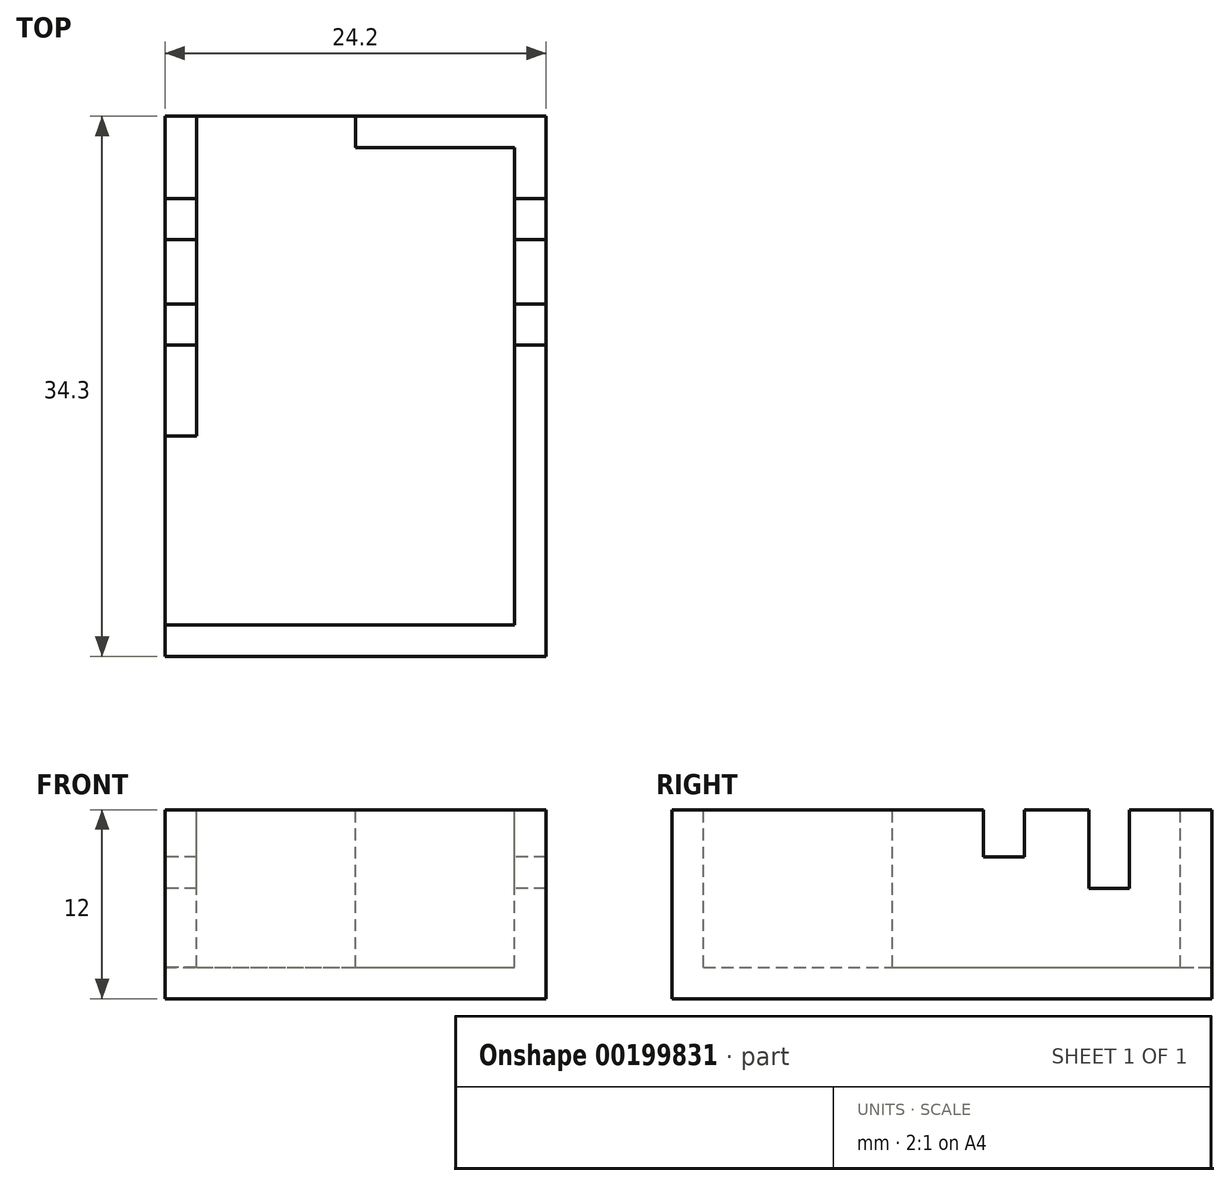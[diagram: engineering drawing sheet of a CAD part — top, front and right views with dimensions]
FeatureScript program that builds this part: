
annotation { "Feature Type Name" : "Feature", "Feature Type Description" : "" }
export const myFeature = defineFeature(function(context is Context, id is Id, definition is map)
    precondition{}
    {
        {
            var Q0;
            Q0=qCreatedBy(makeId("Top.planeOp"),FACE);
            var sketch = newSketch(context, id + "F0", { "sketchPlane" : qUnion([Q0])});
            skLineSegment(sketch, "E0.bottom", {"start": v(0, 0) * mm, "end": v(24.2, 0) * mm});
            skLineSegment(sketch, "E0.top", {"start": v(0, 34.3) * mm, "end": v(24.2, 34.3) * mm});
            skLineSegment(sketch, "E0.left", {"start": v(0, 0) * mm, "end": v(0, 34.3) * mm});
            skLineSegment(sketch, "E0.right", {"start": v(24.2, 0) * mm, "end": v(24.2, 34.3) * mm});
            skSolve(sketch);
        }
        {
            var Q0;
            Q0=makeQuery(id+"F0.imprint","IMPRINT",FACE,{"disambiguationData":[TD([[makeQuery(id+"F0.imprint","IMPRINT",EDGE,{"derivedFrom":sQuery(id+"F0.wireOp",EDGE,"E0.bottom")}),1.0]])]});
            extrude(context, id + "F1", {"entities" : qUnion([Q0]), "depth" : 12 * mm});
        }
        {
            var Q0;
            Q0=makeQuery(id+"F1.opExtrude","CAP_FACE",FACE,{"disambiguationData":[OSD([sQuery(id+"F0.wireOp",EDGE,"E0.bottom"),sQuery(id+"F0.wireOp",EDGE,"E0.top"),sQuery(id+"F0.wireOp",EDGE,"E0.left"),sQuery(id+"F0.wireOp",EDGE,"E0.right")])],"isStart":false});
            var sketch = newSketch(context, id + "F2", { "sketchPlane" : qUnion([Q0])});
            skLineSegment(sketch, "E1.0", {"start": v(2, 32.3) * mm, "end": v(22.2, 32.3) * mm});
            skLineSegment(sketch, "E1.1", {"start": v(2, 2) * mm, "end": v(2, 32.3) * mm});
            skLineSegment(sketch, "E1.2", {"start": v(2, 2) * mm, "end": v(22.2, 2) * mm});
            skLineSegment(sketch, "E1.3", {"start": v(22.2, 2) * mm, "end": v(22.2, 32.3) * mm});
            skSolve(sketch);
        }
        {
            var Q0;
            Q0 = qSketchRegion(id + "F2", true);
            extrude(context, id + "F3", {"entities" : qUnion([Q0]), "operationType" : NewBodyOperationType.REMOVE, "oppositeDirection" : true, "depth" : 10 * mm});
        }
        {
            var Q0;
            Q0=makeQuery(id+"F1.opExtrude","CAP_FACE",FACE,{"disambiguationData":[OSD([sQuery(id+"F0.wireOp",EDGE,"E0.bottom"),sQuery(id+"F0.wireOp",EDGE,"E0.top"),sQuery(id+"F0.wireOp",EDGE,"E0.left"),sQuery(id+"F0.wireOp",EDGE,"E0.right")])],"isStart":false});
            var sketch = newSketch(context, id + "F4", { "sketchPlane" : qUnion([Q0])});
            skLineSegment(sketch, "E2.bottom", {"start": v(2, 2) * mm, "end": v(0, 2) * mm});
            skLineSegment(sketch, "E2.top", {"start": v(2, 14) * mm, "end": v(0, 14) * mm});
            skLineSegment(sketch, "E2.left", {"start": v(2, 2) * mm, "end": v(2, 14) * mm});
            skLineSegment(sketch, "E2.right", {"start": v(0, 2) * mm, "end": v(0, 14) * mm});
            skSolve(sketch);
        }
        {
            var Q0;
            Q0 = qSketchRegion(id + "F4", true);
            extrude(context, id + "F5", {"entities" : qUnion([Q0]), "operationType" : NewBodyOperationType.REMOVE, "oppositeDirection" : true, "depth" : 10 * mm});
        }
        {
            var Q0;
            Q0=makeQuery(id+"F1.opExtrude","CAP_FACE",FACE,{"disambiguationData":[OSD([sQuery(id+"F0.wireOp",EDGE,"E0.bottom"),sQuery(id+"F0.wireOp",EDGE,"E0.top"),sQuery(id+"F0.wireOp",EDGE,"E0.left"),sQuery(id+"F0.wireOp",EDGE,"E0.right")])],"isStart":false});
            var sketch = newSketch(context, id + "F6", { "sketchPlane" : qUnion([Q0])});
            skLineSegment(sketch, "E3.bottom", {"start": v(2, 32.3) * mm, "end": v(12.1, 32.3) * mm});
            skLineSegment(sketch, "E3.top", {"start": v(2, 34.3) * mm, "end": v(12.1, 34.3) * mm});
            skLineSegment(sketch, "E3.left", {"start": v(2, 32.3) * mm, "end": v(2, 34.3) * mm});
            skLineSegment(sketch, "E3.right", {"start": v(12.1, 32.3) * mm, "end": v(12.1, 34.3) * mm});
            skSolve(sketch);
        }
        {
            var Q0;
            Q0 = qSketchRegion(id + "F6", true);
            extrude(context, id + "F7", {"entities" : qUnion([Q0]), "operationType" : NewBodyOperationType.REMOVE, "oppositeDirection" : true, "depth" : 10 * mm});
        }
        {
            var Q0;
            {var subQ0=sQuery(id+"F0.wireOp",EDGE,"E0.right");var subQ1=sQuery(id+"F0.wireOp",EDGE,"E0.left");var subQ2=sQuery(id+"F0.wireOp",EDGE,"E0.top");var subQ3=sQuery(id+"F0.wireOp",EDGE,"E0.bottom");Q0=makeQuery(id+"F7.boolean.opBoolean","SPLIT",FACE,{"disambiguationData":[TD([makeQuery(id+"F1.opExtrude","SWEPT_FACE",FACE,{"disambiguationData":[OSD([subQ3])]})])],"derivedFrom":makeQuery(id+"F1.opExtrude","CAP_FACE",FACE,{"disambiguationData":[OSD([subQ3,subQ2,subQ1,subQ0])],"isStart":false})});}
            var sketch = newSketch(context, id + "F8", { "sketchPlane" : qUnion([Q0])});
            skLineSegment(sketch, "E4.bottom", {"start": v(24.2, 29.07) * mm, "end": v(0, 29.07) * mm});
            skLineSegment(sketch, "E4.top", {"start": v(24.2, 26.47) * mm, "end": v(0, 26.47) * mm});
            skLineSegment(sketch, "E4.left", {"start": v(24.2, 29.07) * mm, "end": v(24.2, 26.47) * mm});
            skLineSegment(sketch, "E4.right", {"start": v(0, 29.07) * mm, "end": v(0, 26.47) * mm});
            skSolve(sketch);
        }
        {
            var Q0;
            Q0 = qSketchRegion(id + "F8", true);
            extrude(context, id + "F9", {"entities" : qUnion([Q0]), "operationType" : NewBodyOperationType.REMOVE, "oppositeDirection" : true, "depth" : 5 * mm});
        }
        {
            var Q0;
            {var subQ1=sQuery(id+"F0.wireOp",EDGE,"E0.right");var subQ3=sQuery(id+"F0.wireOp",EDGE,"E0.left");var subQ5=sQuery(id+"F0.wireOp",EDGE,"E0.bottom");var subQ6=makeQuery(id+"F1.opExtrude","SWEPT_FACE",FACE,{"disambiguationData":[OSD([subQ5])]});var subQ9=sQuery(id+"F0.wireOp",EDGE,"E0.top");Q0=makeQuery(id+"F9.boolean.opBoolean","SPLIT",FACE,{"disambiguationData":[TD([subQ6])],"derivedFrom":makeQuery(id+"F7.boolean.opBoolean","SPLIT",FACE,{"disambiguationData":[TD([subQ6])],"derivedFrom":makeQuery(id+"F1.opExtrude","CAP_FACE",FACE,{"disambiguationData":[OSD([subQ5,subQ9,subQ3,subQ1])],"isStart":false})})});}
            var sketch = newSketch(context, id + "F10", { "sketchPlane" : qUnion([Q0])});
            skLineSegment(sketch, "E5.bottom", {"start": v(24.2, 22.38) * mm, "end": v(0, 22.38) * mm});
            skLineSegment(sketch, "E5.top", {"start": v(24.2, 19.78) * mm, "end": v(0, 19.78) * mm});
            skLineSegment(sketch, "E5.left", {"start": v(24.2, 22.38) * mm, "end": v(24.2, 19.78) * mm});
            skLineSegment(sketch, "E5.right", {"start": v(0, 22.38) * mm, "end": v(0, 19.78) * mm});
            skSolve(sketch);
        }
        {
            var Q0;
            Q0 = qSketchRegion(id + "F10", true);
            extrude(context, id + "F11", {"entities" : qUnion([Q0]), "operationType" : NewBodyOperationType.REMOVE, "oppositeDirection" : true, "depth" : 3 * mm});
        }
    });
